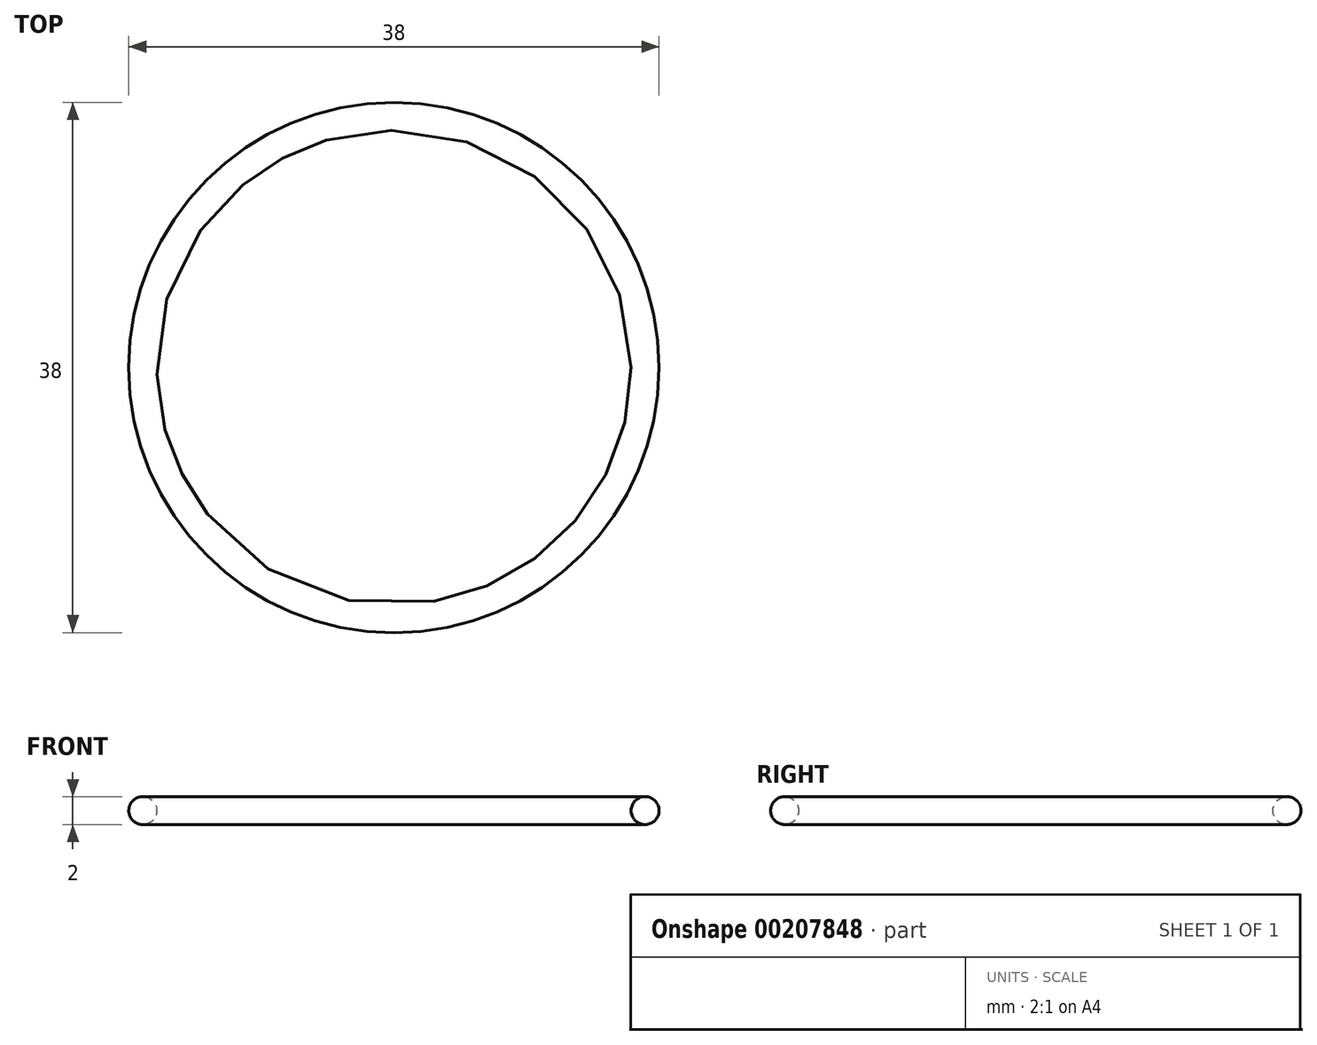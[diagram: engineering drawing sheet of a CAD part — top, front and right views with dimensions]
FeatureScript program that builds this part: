
annotation { "Feature Type Name" : "Feature", "Feature Type Description" : "" }
export const myFeature = defineFeature(function(context is Context, id is Id, definition is map)
    precondition{}
    {
        {
            var Q0;
            Q0=qCreatedBy(makeId("Front.planeOp"),FACE);
            var sketch = newSketch(context, id + "F0", { "sketchPlane" : qUnion([Q0])});
            skCircle(sketch, "E0", {"center": v(-18, 0) * mm, "radius": 1 * mm});
            skLineSegment(sketch, "E1", {"start": v(0, 1) * mm, "end": v(0, -1.87) * mm});
            skSolve(sketch);
        }
        {
            var Q0;
            Q0=makeQuery(id+"F0.imprint","IMPRINT",FACE,{"disambiguationData":[TD([[makeQuery(id+"F0.imprint","IMPRINT",EDGE,{"derivedFrom":sQuery(id+"F0.wireOp",EDGE,"E0")}),1.0]])]});
            var Q1;
            Q1=sQuery(id+"F0.wireOp",EDGE,"E1");
            revolve(context, id + "F1", {"entities" : qUnion([Q0]), "axis" : qUnion([Q1]), "revolveType" : RevolveType.FULL});
        }
    });
